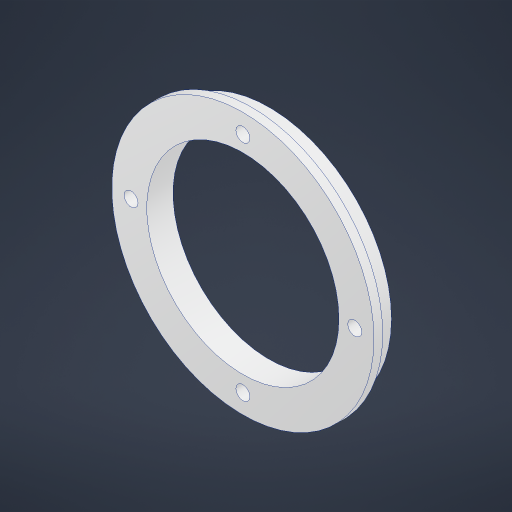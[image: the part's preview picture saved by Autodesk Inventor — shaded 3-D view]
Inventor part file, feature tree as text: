
AUTODESK INVENTOR PART (.ipt)
format: ipt  version: 2023.4 (Build 274418000, 418)  size: 349,696 bytes
history: native  units: in
note: dims shown in document units (in); Inventor stores cm internally (conversion verified against a paired STEP export)
features: sketch x4, extrude x2, hole x2
ambient origin geometry x8: Origin, YZ Plane, XZ Plane, XY Plane, X Axis, Y Axis, Z Axis, Center Point
bodies: Solid1 (feature_tree)
feature tree (8):
  extrude  "Extrusion1"  Depth=0.25in TaperAngle=0.0deg
  hole  "Hole1"  [1 undecoded]
  extrude  "Extrusion4"  Depth=0.25in
  hole  "Hole2"  [1 undecoded]
  sketch  "Sketch1"  dims[d0=3.5in d2=0.25in d3=0.0in]
  sketch  "Sketch3"  dims[d4=3.26in d5=45.0deg]
  sketch  "Sketch7"  dims[d6=1.5748in d8=360.0deg]
  sketch  "Sketch8"  dims[d10=0.156in d11=0.38in d12=0.375in d13=0.25in d14=0.5635in d15=1.0in d16=0.8108in d20=2.75in d25=3.75in d26=0.125in d27=0.0in d28=3.2in d29=0.201in d30=0.75in d31=0.375in d32=0.25in d33=0.5635in d34=0.16in d35=0.0in d36=1.5748in d38=360.0deg]
note: 2 required parameter values undecoded (feature->parameter linkage not recoverable at this tier; creation-order binding heuristic only, values carry confidence <= 0.55)
